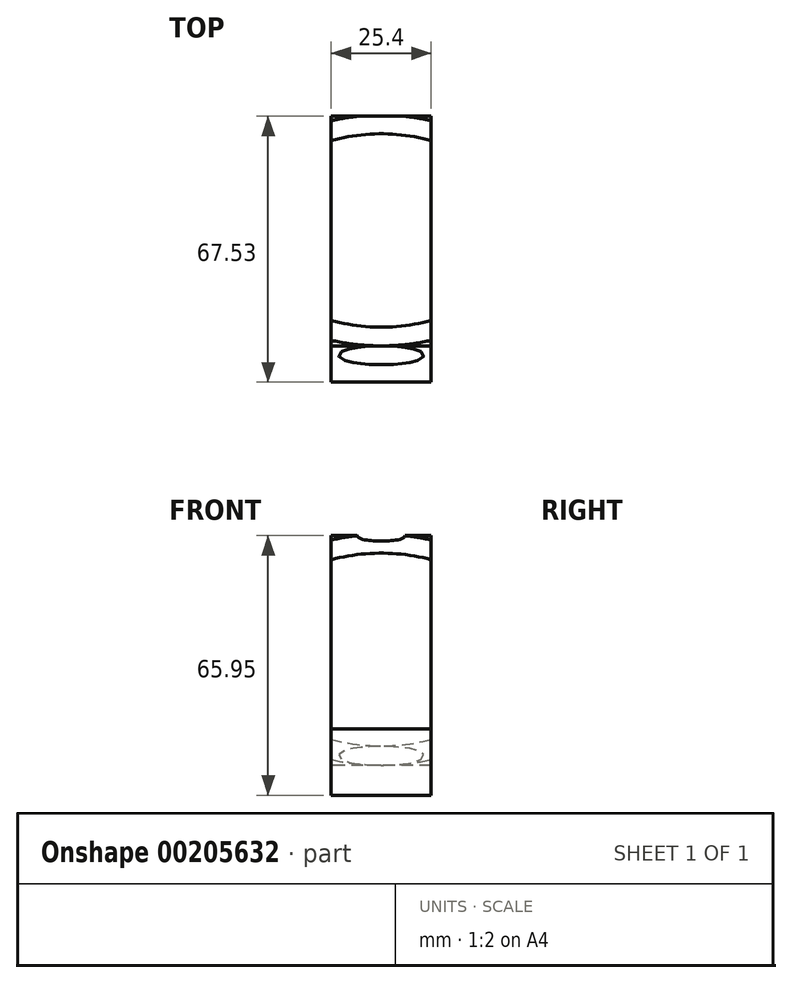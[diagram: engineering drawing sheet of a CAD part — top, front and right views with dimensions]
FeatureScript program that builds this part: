
annotation { "Feature Type Name" : "Feature", "Feature Type Description" : "" }
export const myFeature = defineFeature(function(context is Context, id is Id, definition is map)
    precondition{}
    {
        {
            var Q0;
            Q0=qCreatedBy(makeId("Right.planeOp"),FACE);
            var sketch = newSketch(context, id + "F0", { "sketchPlane" : qUnion([Q0])});
            skLineSegment(sketch, "E0", {"start": v(0, 0) * mm, "end": v(67.53, 0) * mm});
            skLineSegment(sketch, "E1", {"start": v(67.53, 0) * mm, "end": v(67.53, 53.88) * mm});
            skLineSegment(sketch, "E2", {"start": v(67.53, 53.88) * mm, "end": v(13.65, 0) * mm});
            skLineSegment(sketch, "E3", {"start": v(13.65, 0) * mm, "end": v(0, 13.65) * mm});
            skLineSegment(sketch, "E4", {"start": v(0, 13.65) * mm, "end": v(0, 0) * mm});
            skLineSegment(sketch, "E5", {"start": v(67.53, 0) * mm, "end": v(67.53, -3.17) * mm});
            skLineSegment(sketch, "E6", {"start": v(67.53, -3.17) * mm, "end": v(0, -3.18) * mm});
            skLineSegment(sketch, "E7", {"start": v(0, -3.18) * mm, "end": v(0, 0) * mm});
            skLineSegment(sketch, "E8", {"start": v(13.65, 0) * mm, "end": v(9.2, 4.45) * mm});
            skLineSegment(sketch, "E9", {"start": v(9.2, 4.45) * mm, "end": v(63.09, 58.33) * mm});
            skLineSegment(sketch, "E10", {"start": v(63.09, 58.33) * mm, "end": v(67.53, 53.88) * mm});
            skLineSegment(sketch, "E11", {"start": v(63.09, 58.33) * mm, "end": v(67.53, 62.77) * mm});
            skLineSegment(sketch, "E12", {"start": v(67.53, 62.77) * mm, "end": v(67.53, 53.88) * mm});
            skSolve(sketch);
        }
        {
            var Q0;
            Q0 = qSketchRegion(id + "F0", true);
            extrude(context, id + "F1", {"entities" : qUnion([Q0]), "depth" : 12.7 * mm, "hasSecondDirection" : true, "secondDirectionOppositeDirection" : true, "secondDirectionDepth" : 12.7 * mm});
        }
        {
            var Q0;
            Q0=qCreatedBy(makeId("Right.planeOp"),FACE);
            var sketch = newSketch(context, id + "F2", { "sketchPlane" : qUnion([Q0])});
            skLineSegment(sketch, "E13", {"start": v(0, 0) * mm, "end": v(9.2, 0) * mm, "construction": true});
            skLineSegment(sketch, "E14", {"start": v(9.2, 0) * mm, "end": v(9.2, 9.2) * mm, "construction": true});
            skLineSegment(sketch, "E15", {"start": v(9.2, 9.2) * mm, "end": v(36.15, 9.2) * mm, "construction": true});
            skLineSegment(sketch, "E16", {"start": v(36.15, 9.2) * mm, "end": v(36.15, 36.15) * mm, "construction": true});
            skLineSegment(sketch, "E17", {"start": v(36.15, 36.15) * mm, "end": v(9.2, 9.2) * mm, "construction": true});
            skCircle(sketch, "E18", {"center": v(9.2, 9.2) * mm, "radius": 4.76 * mm});
            skLineSegment(sketch, "E19", {"start": v(36.15, 36.15) * mm, "end": v(24, 48.3) * mm, "construction": true});
            skSolve(sketch);
        }
        {
            var Q0;
            Q0 = qSketchRegion(id + "F2", true);
            var Q1;
            Q1=sQuery(id+"F2.wireOp",EDGE,"E19");
            revolve(context, id + "F3", {"operationType" : NewBodyOperationType.REMOVE, "entities" : qUnion([Q0]), "axis" : qUnion([Q1]), "revolveType" : RevolveType.FULL, "oppositeDirection" : true});
        }
    });
